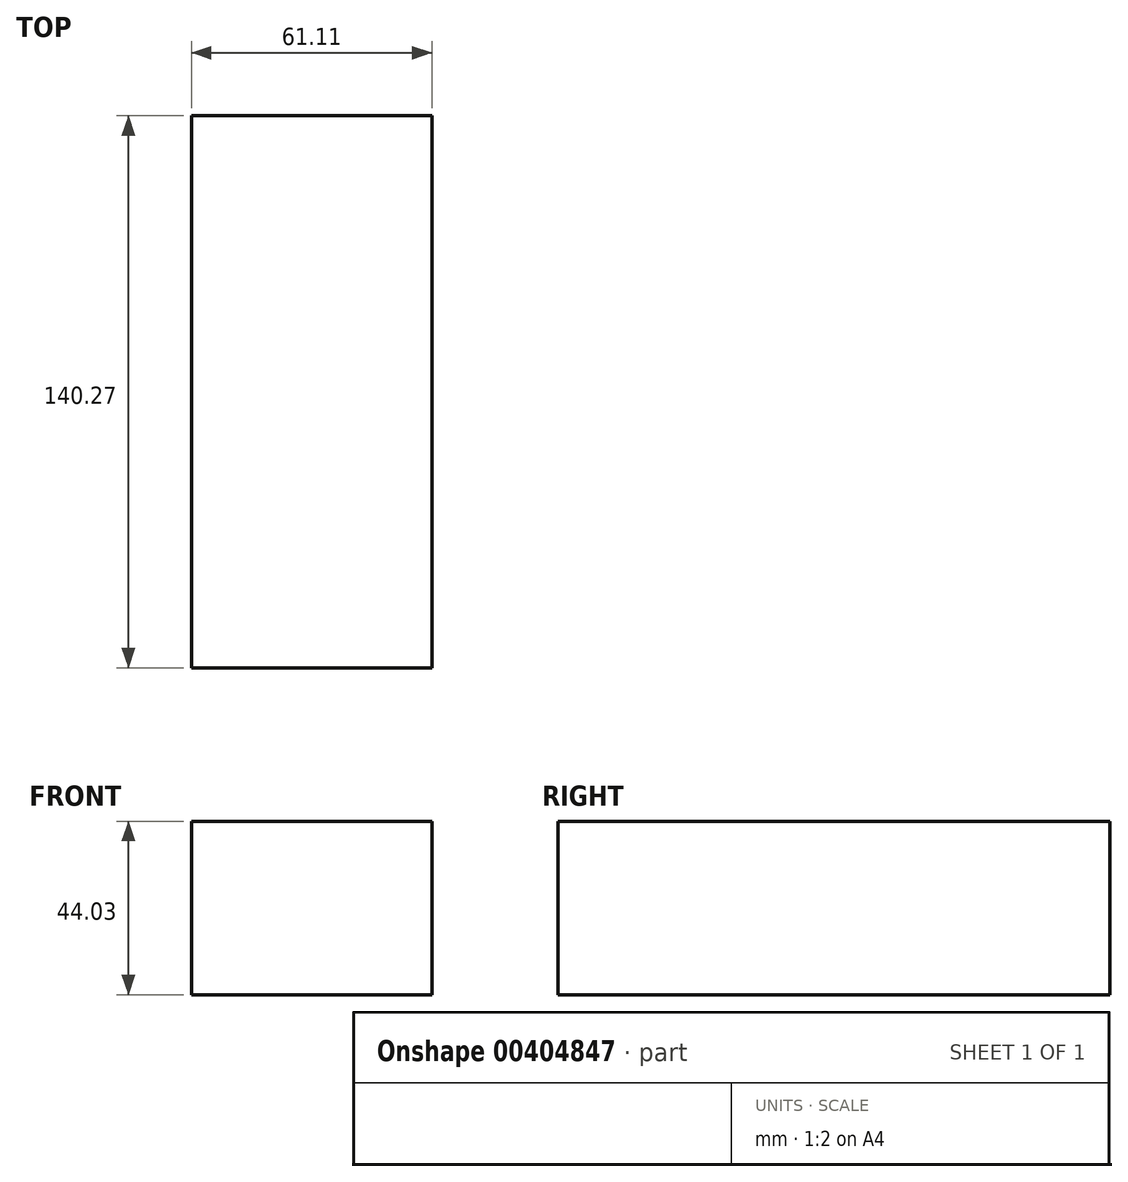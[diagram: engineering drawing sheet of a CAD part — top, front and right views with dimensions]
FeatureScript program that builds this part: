
annotation { "Feature Type Name" : "Feature", "Feature Type Description" : "" }
export const myFeature = defineFeature(function(context is Context, id is Id, definition is map)
    precondition{}
    {
        {
            var Q0;
            Q0=qCreatedBy(makeId("Front.planeOp"),FACE);
            var sketch = newSketch(context, id + "F0", { "sketchPlane" : qUnion([Q0])});
            skLineSegment(sketch, "E0.bottom", {"start": v(38, -28.74) * mm, "end": v(-23.1, -28.74) * mm});
            skLineSegment(sketch, "E0.top", {"start": v(38, 15.29) * mm, "end": v(-23.1, 15.29) * mm});
            skLineSegment(sketch, "E0.left", {"start": v(38, -28.74) * mm, "end": v(38, 15.29) * mm});
            skLineSegment(sketch, "E0.right", {"start": v(-23.1, -28.74) * mm, "end": v(-23.1, 15.29) * mm});
            skSolve(sketch);
        }
        {
            var Q0;
            Q0 = qSketchRegion(id + "F0", true);
            extrude(context, id + "F1", {"entities" : qUnion([Q0]), "oppositeDirection" : true, "depth" : 140.27 * mm});
        }
    });
